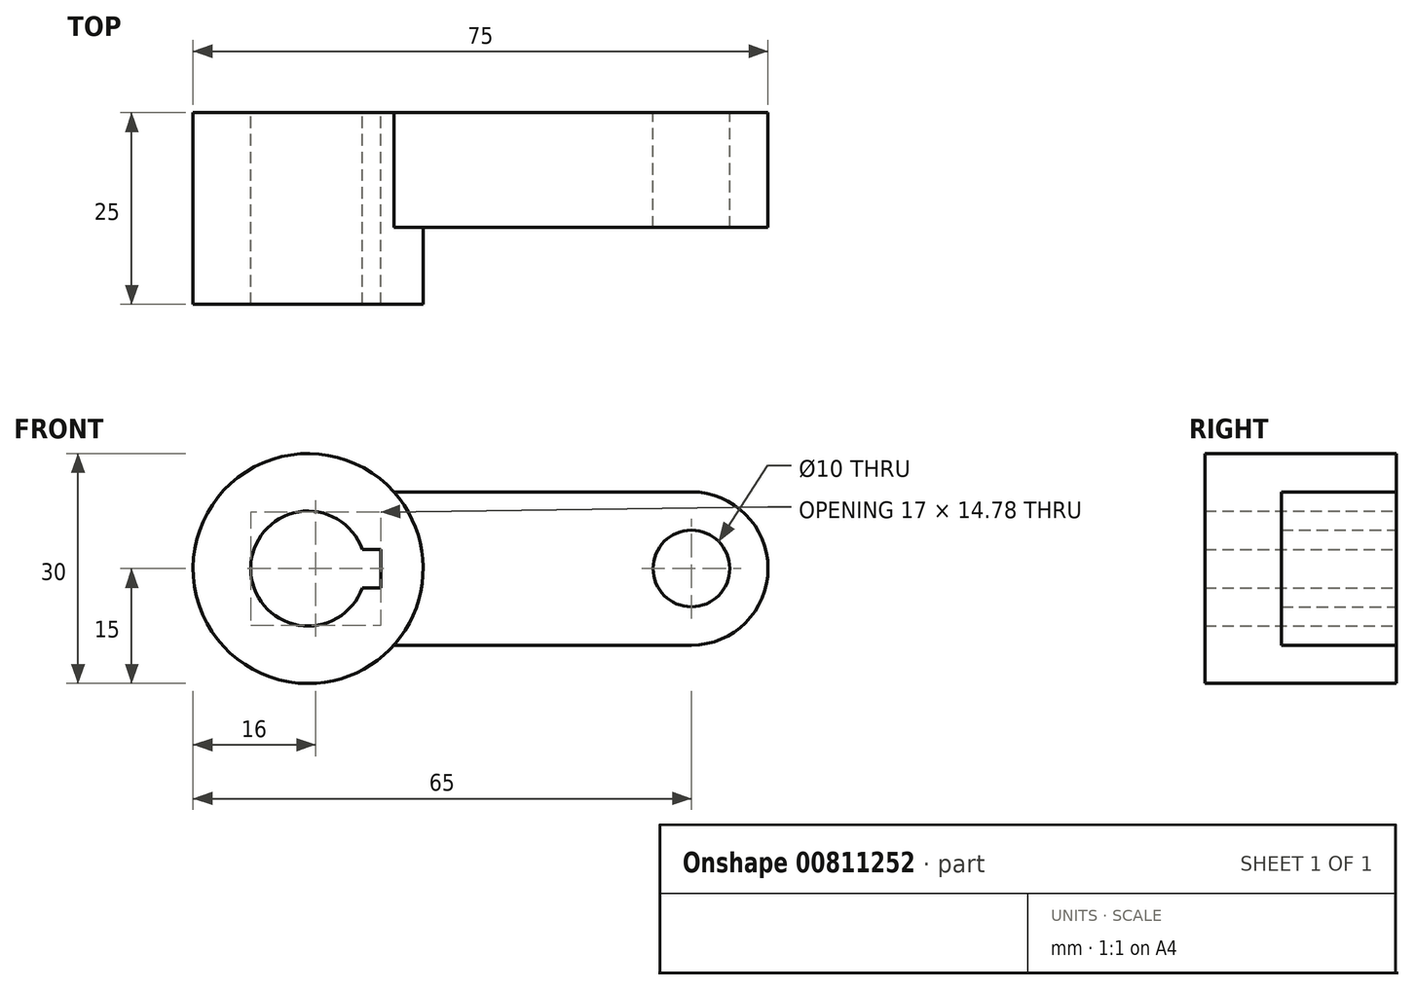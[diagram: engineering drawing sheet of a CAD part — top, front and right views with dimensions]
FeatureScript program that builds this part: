
annotation { "Feature Type Name" : "Feature", "Feature Type Description" : "" }
export const myFeature = defineFeature(function(context is Context, id is Id, definition is map)
    precondition{}
    {
        {
            var Q0;
            Q0=qCreatedBy(makeId("Front.planeOp"),FACE);
            var sketch = newSketch(context, id + "F0", { "sketchPlane" : qUnion([Q0])});
            skCircle(sketch, "E0", {"center": v(0, 0) * mm, "radius": 15 * mm});
            skArc(sketch, "E1", {"start": v(7.07, 2.5) * mm, "mid": v(-7.5, 0) * mm, "end": v(7.07, -2.5) * mm});
            skLineSegment(sketch, "E2", {"start": v(0, 0) * mm, "end": v(50, 0) * mm, "construction": true});
            skCircle(sketch, "E3", {"center": v(50, 0) * mm, "radius": 5 * mm});
            skArc(sketch, "E4", {"start": v(50, -10) * mm, "mid": v(60, 0) * mm, "end": v(50, 10) * mm});
            skLineSegment(sketch, "E5", {"start": v(50, 10) * mm, "end": v(11.18, 10) * mm});
            skLineSegment(sketch, "E6.MirrorCS", {"start": v(50, -10) * mm, "end": v(11.18, -10) * mm});
            skLineSegment(sketch, "E7", {"start": v(7.07, 2.5) * mm, "end": v(9.5, 2.5) * mm});
            skLineSegment(sketch, "E8", {"start": v(9.5, 2.5) * mm, "end": v(9.5, 0) * mm});
            skLineSegment(sketch, "E9.MirrorCS", {"start": v(9.5, -2.5) * mm, "end": v(9.5, 0) * mm});
            skLineSegment(sketch, "E10.MirrorCS", {"start": v(7.07, -2.5) * mm, "end": v(9.5, -2.5) * mm});
            skSolve(sketch);
        }
        {
            var Q0;
            Q0 = qSketchRegion(id + "F0", true);
            extrude(context, id + "F1", {"entities" : qUnion([Q0]), "depth" : 15 * mm, "offsetDistance" : 25 * mm});
        }
        {
            var Q0;
            Q0=makeQuery(id+"F0.imprint","IMPRINT",FACE,{"disambiguationData":[TD([[makeQuery(id+"F0.imprint","IMPRINT",EDGE,{"derivedFrom":sQuery(id+"F0.wireOp",EDGE,"E1")}),-1.0]])]});
            extrude(context, id + "F2", {"entities" : qUnion([Q0]), "operationType" : NewBodyOperationType.ADD, "depth" : 25 * mm, "offsetDistance" : 25 * mm});
        }
    });
